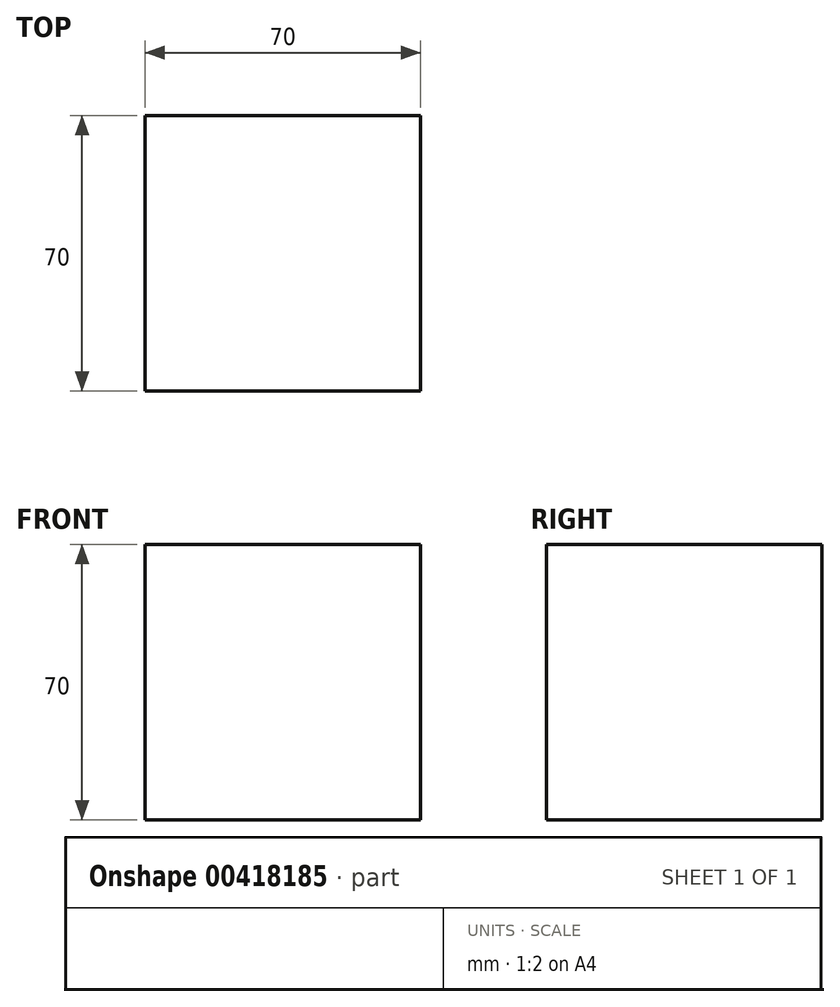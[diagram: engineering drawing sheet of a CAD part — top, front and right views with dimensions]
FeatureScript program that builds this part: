
annotation { "Feature Type Name" : "Feature", "Feature Type Description" : "" }
export const myFeature = defineFeature(function(context is Context, id is Id, definition is map)
    precondition{}
    {
        {
            var Q0;
            Q0=qCreatedBy(makeId("Top.planeOp"),FACE);
            var sketch = newSketch(context, id + "F0", { "sketchPlane" : qUnion([Q0])});
            skLineSegment(sketch, "E0.bottom", {"start": v(-29.5, -22.03) * mm, "end": v(40.5, -22.03) * mm});
            skLineSegment(sketch, "E0.top", {"start": v(-29.5, 47.97) * mm, "end": v(40.5, 47.97) * mm});
            skLineSegment(sketch, "E0.left", {"start": v(-29.5, -22.03) * mm, "end": v(-29.5, 47.97) * mm});
            skLineSegment(sketch, "E0.right", {"start": v(40.5, -22.03) * mm, "end": v(40.5, 47.97) * mm});
            skPoint(sketch, "E0.middle", {"position": v(5.5, 12.97) * mm});
            skSolve(sketch);
        }
        {
            var Q0;
            Q0 = qSketchRegion(id + "F0", true);
            extrude(context, id + "F1", {"entities" : qUnion([Q0]), "depth" : 70 * mm});
        }
    });
